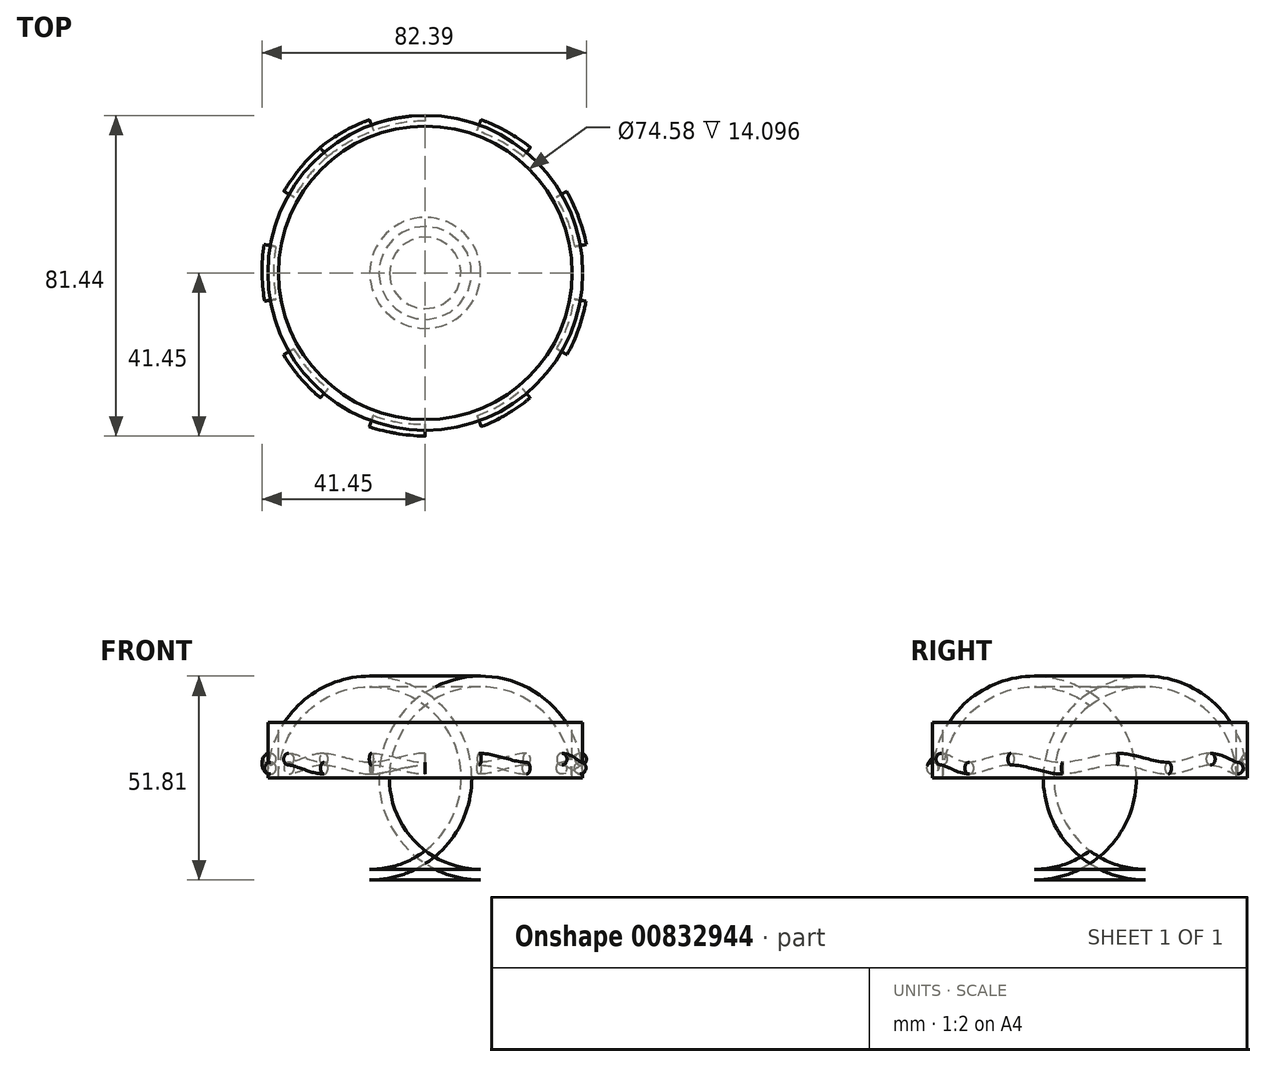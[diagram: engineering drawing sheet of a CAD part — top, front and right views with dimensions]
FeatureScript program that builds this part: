
annotation { "Feature Type Name" : "Feature", "Feature Type Description" : "" }
export const myFeature = defineFeature(function(context is Context, id is Id, definition is map)
    precondition{}
    {
        {
            var Q0;
            Q0=qCreatedBy(makeId("Front.planeOp"),FACE);
            var sketch = newSketch(context, id + "F0", { "sketchPlane" : qUnion([Q0])});
            skLineSegment(sketch, "E0", {"start": v(0, 0) * mm, "end": v(-14.09, 0) * mm});
            skArc(sketch, "E1", {"start": v(-40, 25.9) * mm, "mid": v(-32.4, 7.59) * mm, "end": v(-14.09, 0) * mm});
            skLineSegment(sketch, "E2", {"start": v(-40, 25.9) * mm, "end": v(-40, 40) * mm});
            skLineSegment(sketch, "E3.0", {"start": v(-37.3, 25.9) * mm, "end": v(-37.3, 40) * mm});
            skArc(sketch, "E3.1", {"start": v(-37.3, 25.9) * mm, "mid": v(-30.5, 9.5) * mm, "end": v(-14.09, 2.7) * mm});
            skLineSegment(sketch, "E3.2", {"start": v(0, 2.7) * mm, "end": v(-14.09, 2.7) * mm});
            skLineSegment(sketch, "E4", {"start": v(-40, 40) * mm, "end": v(-37.3, 40) * mm});
            skLineSegment(sketch, "E5", {"start": v(0, 2.7) * mm, "end": v(0, 0) * mm});
            skSolve(sketch);
        }
        {
            var Q0;
            Q0 = qSketchRegion(id + "F0", true);
            var Q1;
            Q1=sQuery(id+"F0.wireOp",EDGE,"E5");
            revolve(context, id + "F1", {"surfaceOperationType" : NewSurfaceOperationType.NEW, "entities" : qUnion([Q0]), "axis" : qUnion([Q1]), "revolveType" : RevolveType.FULL});
        }
        {
            var Q0;
            Q0=qCreatedBy(makeId("Right.planeOp"),FACE);
            var sketch = newSketch(context, id + "F2", { "sketchPlane" : qUnion([Q0])});
            skCircle(sketch, "E6", {"center": v(40.07, 30.7) * mm, "radius": 1.5 * mm});
            skSolve(sketch);
        }
        {
            var Q0;
            Q0=qCreatedBy(makeId("Right.planeOp"),FACE);
            var sketch = newSketch(context, id + "F3", { "sketchPlane" : qUnion([Q0])});
            skLineSegment(sketch, "E7", {"start": v(0, 0) * mm, "end": v(0, 57.86) * mm, "construction": true});
            skSolve(sketch);
        }
        {
            var Q0;
            Q0=qCreatedBy(makeId("Right.planeOp"),FACE);
            var Q1;
            Q1=sQuery(id+"F3.wireOp",EDGE,"E7");
            cPlane(context, id + "F4", {"entities" : qUnion([Q0, Q1]), "cplaneType" : CPlaneType.LINE_ANGLE, "offset" : 25 * mm, "angle" : 20 * degree, "width" : 150 * mm, "height" : 150 * mm});
        }
        {
            var Q0;
            Q0=qCreatedBy(id+"F4.planeOp",FACE);
            var sketch = newSketch(context, id + "F5", { "sketchPlane" : qUnion([Q0])});
            skCircle(sketch, "E8", {"center": v(-39.95, 28.42) * mm, "radius": 1.5 * mm});
            skSolve(sketch);
        }
        {
            var Q1;
            Q1=makeQuery(id+"F5.imprint","IMPRINT",FACE,{"disambiguationData":[TD([[makeQuery(id+"F5.imprint","IMPRINT",EDGE,{"derivedFrom":sQuery(id+"F5.wireOp",EDGE,"E8")}),1.0]])]});
            var Q2;
            Q2=makeQuery(id+"F2.imprint","IMPRINT",FACE,{"disambiguationData":[TD([[makeQuery(id+"F2.imprint","IMPRINT",EDGE,{"derivedFrom":sQuery(id+"F2.wireOp",EDGE,"E6")}),1.0]])]});
            loft(context, id + "F6", {"startCondition" : LoftEndDerivativeType.NORMAL_TO_PROFILE, "startMagnitude" : 1, "endCondition" : LoftEndDerivativeType.NORMAL_TO_PROFILE, "endMagnitude" : 1, "sheetProfilesArray" : [{ "sheetProfileEntities" : qUnion([Q1]) }, { "sheetProfileEntities" : qUnion([Q2]) }]});
        }
        {
            var Q0;
            Q0=makeQuery(id+"F6.opLoft","SWEPT_BODY",BODY,{"disambiguationData":[OSD([makeQuery(id+"F2.imprint","IMPRINT",FACE,{"disambiguationData":[TD([[makeQuery(id+"F2.imprint","IMPRINT",EDGE,{"derivedFrom":sQuery(id+"F2.wireOp",EDGE,"E6")}),1.0]])]}),makeQuery(id+"F5.imprint","IMPRINT",FACE,{"disambiguationData":[TD([[makeQuery(id+"F5.imprint","IMPRINT",EDGE,{"derivedFrom":sQuery(id+"F5.wireOp",EDGE,"E8")}),1.0]])]})])]});
            var Q1;
            Q1=makeQuery(id+"F6.opLoft","CAP_FACE",FACE,{"disambiguationData":[OSD([makeQuery(id+"F5.imprint","IMPRINT",FACE,{"disambiguationData":[TD([[makeQuery(id+"F5.imprint","IMPRINT",EDGE,{"derivedFrom":sQuery(id+"F5.wireOp",EDGE,"E8")}),1.0]])]})])],"isStart":true});
            mirror(context, id + "F7", {"entities" : qUnion([Q0]), "mirrorPlane" : qUnion([Q1])});
        }
        {
            var Q0;
            Q0=makeQuery(id+"F6.opLoft","SWEPT_BODY",BODY,{"disambiguationData":[OSD([makeQuery(id+"F2.imprint","IMPRINT",FACE,{"disambiguationData":[TD([[makeQuery(id+"F2.imprint","IMPRINT",EDGE,{"derivedFrom":sQuery(id+"F2.wireOp",EDGE,"E6")}),1.0]])]}),makeQuery(id+"F5.imprint","IMPRINT",FACE,{"disambiguationData":[TD([[makeQuery(id+"F5.imprint","IMPRINT",EDGE,{"derivedFrom":sQuery(id+"F5.wireOp",EDGE,"E8")}),1.0]])]})])]});
            var Q1;
            Q1=sQuery(id+"F3.wireOp",EDGE,"E7");
            circularPattern(context, id + "F8", {"entities" : qUnion([Q0]), "axis" : qUnion([Q1]), "angle" : 360 * degree, "instanceCount" : 9, "equalSpace" : true});
        }
        {
            var Q0;
            Q0=makeQuery(id+"F6.opLoft","SWEPT_BODY",BODY,{"disambiguationData":[OSD([makeQuery(id+"F2.imprint","IMPRINT",FACE,{"disambiguationData":[TD([[makeQuery(id+"F2.imprint","IMPRINT",EDGE,{"derivedFrom":sQuery(id+"F2.wireOp",EDGE,"E6")}),1.0]])]}),makeQuery(id+"F5.imprint","IMPRINT",FACE,{"disambiguationData":[TD([[makeQuery(id+"F5.imprint","IMPRINT",EDGE,{"derivedFrom":sQuery(id+"F5.wireOp",EDGE,"E8")}),1.0]])]})])]});
            var Q1;
            Q1=makeQuery(id+"F1.opRevolve","SWEPT_BODY",BODY,{"disambiguationData":[OSD([sQuery(id+"F0.wireOp",EDGE,"E0"),sQuery(id+"F0.wireOp",EDGE,"E1"),sQuery(id+"F0.wireOp",EDGE,"E2"),sQuery(id+"F0.wireOp",EDGE,"E3.0"),sQuery(id+"F0.wireOp",EDGE,"E3.1"),sQuery(id+"F0.wireOp",EDGE,"E3.2"),sQuery(id+"F0.wireOp",EDGE,"E4"),sQuery(id+"F0.wireOp",EDGE,"E5")])]});
            booleanBodies(context, id + "F9", {"operationType" : BooleanOperationType.SUBTRACTION, "tools" : qUnion([Q0]), "targets" : qUnion([Q1]), "keepTools" : true});
        }
        {
            var Q0;
            Q0=makeQuery(id+"F6.opLoft","SWEPT_BODY",BODY,{"disambiguationData":[OSD([makeQuery(id+"F2.imprint","IMPRINT",FACE,{"disambiguationData":[TD([[makeQuery(id+"F2.imprint","IMPRINT",EDGE,{"derivedFrom":sQuery(id+"F2.wireOp",EDGE,"E6")}),1.0]])]}),makeQuery(id+"F5.imprint","IMPRINT",FACE,{"disambiguationData":[TD([[makeQuery(id+"F5.imprint","IMPRINT",EDGE,{"derivedFrom":sQuery(id+"F5.wireOp",EDGE,"E8")}),1.0]])]})])]});
            transform(context, id + "F10", {"entities" : qUnion([Q0]), "transformType" : TransformType.TRANSLATION_3D, "dx" : 0 * mm, "dy" : 0 * mm, "dz" : -19.1 * mm, "makeCopy" : false});
        }
        {
            var Q0;
            Q0=makeQuery(id+"F6.opLoft","SWEPT_BODY",BODY,{"disambiguationData":[OSD([makeQuery(id+"F2.imprint","IMPRINT",FACE,{"disambiguationData":[TD([[makeQuery(id+"F2.imprint","IMPRINT",EDGE,{"derivedFrom":sQuery(id+"F2.wireOp",EDGE,"E6")}),1.0]])]}),makeQuery(id+"F5.imprint","IMPRINT",FACE,{"disambiguationData":[TD([[makeQuery(id+"F5.imprint","IMPRINT",EDGE,{"derivedFrom":sQuery(id+"F5.wireOp",EDGE,"E8")}),1.0]])]})])]});
            var Q1;
            Q1=qCreatedBy(makeId("Origin.pointOp"),VERTEX);
            transform(context, id + "F11", {"entities" : qUnion([Q0]), "transformType" : TransformType.SCALE_UNIFORMLY, "scale" : 0.85, "scalePoint" : qUnion([Q1]), "makeCopy" : false});
        }
        {
            var Q0;
            Q0=makeQuery(id+"F6.opLoft","SWEPT_BODY",BODY,{"disambiguationData":[OSD([makeQuery(id+"F2.imprint","IMPRINT",FACE,{"disambiguationData":[TD([[makeQuery(id+"F2.imprint","IMPRINT",EDGE,{"derivedFrom":sQuery(id+"F2.wireOp",EDGE,"E6")}),1.0]])]}),makeQuery(id+"F5.imprint","IMPRINT",FACE,{"disambiguationData":[TD([[makeQuery(id+"F5.imprint","IMPRINT",EDGE,{"derivedFrom":sQuery(id+"F5.wireOp",EDGE,"E8")}),1.0]])]})])]});
            var Q1;
            Q1=makeQuery(id+"F1.opRevolve","SWEPT_BODY",BODY,{"disambiguationData":[OSD([sQuery(id+"F0.wireOp",EDGE,"E0"),sQuery(id+"F0.wireOp",EDGE,"E1"),sQuery(id+"F0.wireOp",EDGE,"E2"),sQuery(id+"F0.wireOp",EDGE,"E3.0"),sQuery(id+"F0.wireOp",EDGE,"E3.1"),sQuery(id+"F0.wireOp",EDGE,"E3.2"),sQuery(id+"F0.wireOp",EDGE,"E4"),sQuery(id+"F0.wireOp",EDGE,"E5")])]});
            booleanBodies(context, id + "F12", {"operationType" : BooleanOperationType.SUBTRACTION, "tools" : qUnion([Q0]), "targets" : qUnion([Q1])});
        }
    });
